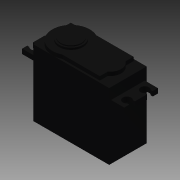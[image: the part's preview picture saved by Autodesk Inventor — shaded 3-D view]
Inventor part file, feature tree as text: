
AUTODESK INVENTOR PART (.ipt)
format: ipt  version: 2016 (Build 200138000, 138)  size: 134,656 bytes
history: native  units: in
note: dims shown in document units (in); Inventor stores cm internally (conversion verified against a paired STEP export)
features: mirror x1, other x1, imported_body x1
ambient origin geometry x8: Origin, YZ Plane, XZ Plane, XY Plane, X Axis, Y Axis, Z Axis, Center Point
bodies: Body1 (feature_tree)
feature tree (3):
  mirror  "Mirror2"
  other  "servo.ipt1"
  imported_body  "Base1"
